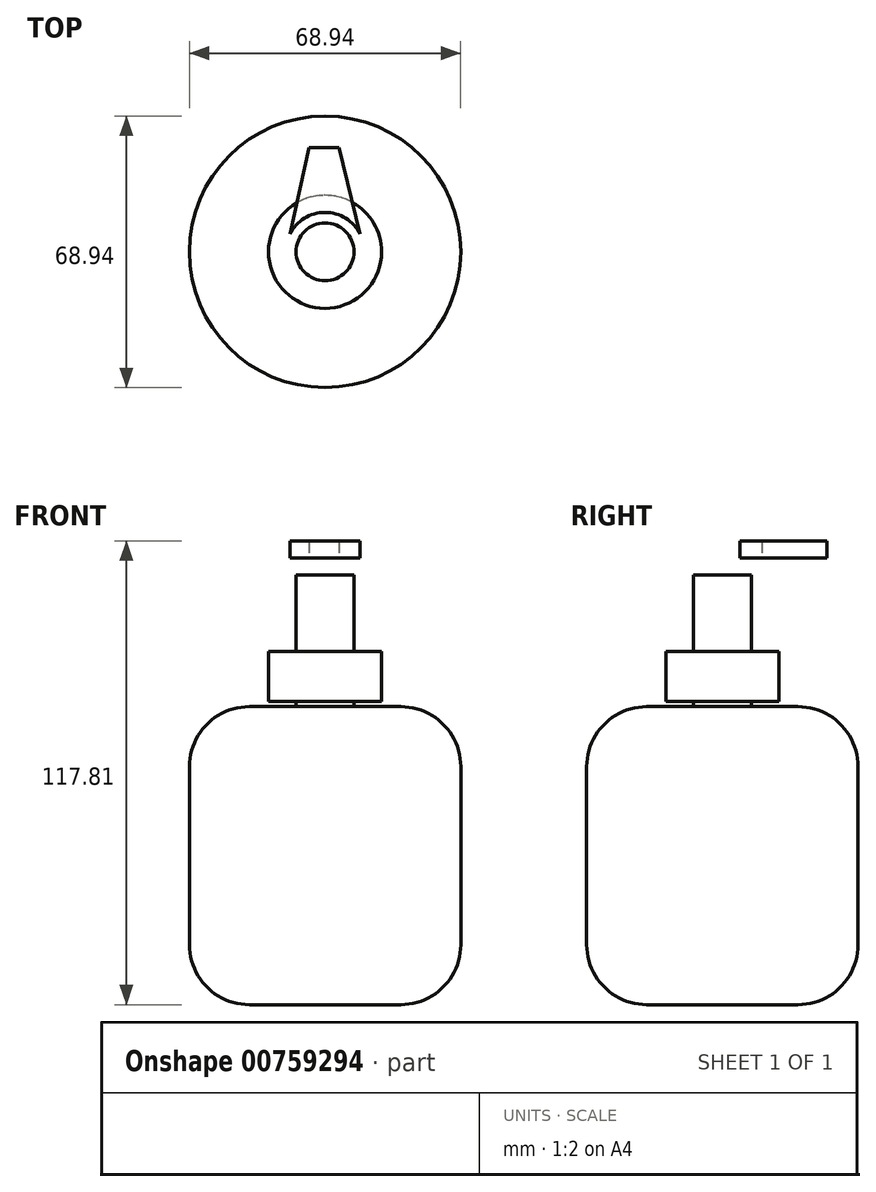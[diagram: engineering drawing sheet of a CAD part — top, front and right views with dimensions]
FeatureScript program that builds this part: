
annotation { "Feature Type Name" : "Feature", "Feature Type Description" : "" }
export const myFeature = defineFeature(function(context is Context, id is Id, definition is map)
    precondition{}
    {
        {
            var Q0;
            Q0=qCreatedBy(makeId("Front.planeOp"),FACE);
            var sketch = newSketch(context, id + "F0", { "sketchPlane" : qUnion([Q0])});
            skLineSegment(sketch, "E0.bottom", {"start": v(0, -0.18) * mm, "end": v(-19.23, -0.18) * mm});
            skLineSegment(sketch, "E0.top", {"start": v(0, -75.9) * mm, "end": v(-19.23, -75.9) * mm});
            skLineSegment(sketch, "E0.left", {"start": v(0, -0.18) * mm, "end": v(0, -75.9) * mm});
            skLineSegment(sketch, "E0.right", {"start": v(-34.47, -15.42) * mm, "end": v(-34.47, -60.66) * mm});
            skPoint(sketch, "E1.visualSharp", {"position": v(-34.47, -0.18) * mm});
            skArc(sketch, "E1.filletArc", {"start": v(-19.23, -0.18) * mm, "mid": v(-30, -4.65) * mm, "end": v(-34.47, -15.42) * mm});
            skPoint(sketch, "E2.visualSharp", {"position": v(-34.47, -75.9) * mm});
            skArc(sketch, "E2.filletArc", {"start": v(-34.47, -60.66) * mm, "mid": v(-30, -71.43) * mm, "end": v(-19.23, -75.9) * mm});
            skLineSegment(sketch, "E3", {"start": v(-7.35, -0.18) * mm, "end": v(-7.35, 1.1) * mm});
            skLineSegment(sketch, "E4", {"start": v(-7.35, 1.1) * mm, "end": v(-14.36, 1.1) * mm});
            skLineSegment(sketch, "E5", {"start": v(-14.36, 1.1) * mm, "end": v(-14.36, 13.9) * mm});
            skLineSegment(sketch, "E6", {"start": v(-14.36, 13.9) * mm, "end": v(-7.35, 13.9) * mm});
            skLineSegment(sketch, "E7", {"start": v(-7.35, 13.9) * mm, "end": v(-7.35, 19.75) * mm});
            skLineSegment(sketch, "E8", {"start": v(-7.35, 19.75) * mm, "end": v(0, 19.75) * mm});
            skLineSegment(sketch, "E9", {"start": v(0, 19.75) * mm, "end": v(0, 0) * mm});
            skPoint(sketch, "E10.orphan", {"position": v(0, 18.47) * mm});
            skLineSegment(sketch, "E11", {"start": v(-7.35, -0.18) * mm, "end": v(0, -0.18) * mm});
            skLineSegment(sketch, "E12", {"start": v(0, 19.75) * mm, "end": v(0, -0.18) * mm});
            skSolve(sketch);
        }
        {
            var Q0;
            Q0 = qSketchRegion(id + "F0", true);
            var Q1;
            Q1=sQuery(id+"F0.wireOp",EDGE,"E9");
            revolve(context, id + "F1", {"surfaceOperationType" : NewSurfaceOperationType.NEW, "entities" : qUnion([Q0]), "axis" : qUnion([Q1]), "revolveType" : RevolveType.FULL});
        }
        {
            var Q0;
            Q0=makeQuery(id+"F1.opRevolve","SWEPT_FACE",FACE,{"disambiguationData":[OSD([sQuery(id+"F0.wireOp",EDGE,"E8")])]});
            extrude(context, id + "F2", {"entities" : qUnion([Q0]), "operationType" : NewBodyOperationType.ADD, "depth" : 13.46 * mm, "offsetDistance" : 25.4 * mm});
        }
        {
            var Q0;
            Q0=qCreatedBy(makeId("Top.planeOp"),FACE);
            cPlane(context, id + "F3", {"entities" : qUnion([Q0]), "cplaneType" : CPlaneType.OFFSET, "offset" : 33.27 * mm, "width" : 152.4 * mm, "height" : 152.4 * mm});
        }
        {
            var Q0;
            Q0=qCreatedBy(id+"F3.planeOp",FACE);
            var sketch = newSketch(context, id + "F4", { "sketchPlane" : qUnion([Q0])});
            skCircle(sketch, "E13", {"center": v(0, 0) * mm, "radius": 10 * mm});
            skLineSegment(sketch, "E14", {"start": v(-8.93, 4.52) * mm, "end": v(-4.11, 26.52) * mm});
            skLineSegment(sketch, "E15", {"start": v(-4.11, 26.52) * mm, "end": v(3.57, 26.52) * mm});
            skLineSegment(sketch, "E16", {"start": v(3.57, 26.52) * mm, "end": v(8.93, 4.52) * mm});
            skSolve(sketch);
        }
        {
            var Q0;
            {var subQ0=sQuery(id+"F4.wireOp",EDGE,"E14");Q0=makeQuery(id+"F4.imprint","IMPRINT",FACE,{"disambiguationData":[TD([[makeQuery(id+"F4.imprint","IMPRINT",EDGE,{"derivedFrom":subQ0}),-1.0]])]});}
            extrude(context, id + "F5", {"entities" : qUnion([Q0]), "depth" : 8.64 * mm, "offsetDistance" : 25.4 * mm});
        }
        {
            var Q0;
            Q0=makeQuery(id+"F5.opExtrude","CAP_FACE",FACE,{"disambiguationData":[OSD([sQuery(id+"F4.wireOp",EDGE,"E13"),sQuery(id+"F4.wireOp",EDGE,"E14"),sQuery(id+"F4.wireOp",EDGE,"E15"),sQuery(id+"F4.wireOp",EDGE,"E16")])],"isStart":true});
            extrude(context, id + "F6", {"entities" : qUnion([Q0]), "operationType" : NewBodyOperationType.REMOVE, "oppositeDirection" : true, "depth" : 4.32 * mm, "offsetDistance" : 25.4 * mm});
        }
        {
            var Q0;
            Q0=sQuery(id+"F4.wireOp",EDGE,"E13");
            extrude(context, id + "F7", {"bodyType" : ToolBodyType.SURFACE, "surfaceEntities" : qUnion([Q0]), "depth" : 10.16 * mm, "offsetDistance" : 25.4 * mm});
        }
    });
